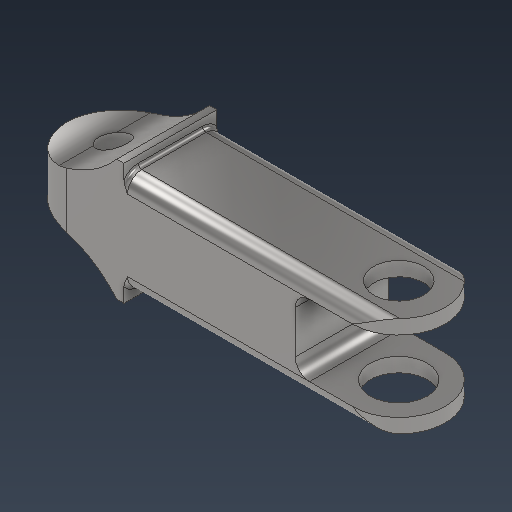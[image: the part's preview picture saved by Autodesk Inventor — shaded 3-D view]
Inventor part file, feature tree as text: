
AUTODESK INVENTOR PART (.ipt)
format: ipt  version: 2021 (Build 250183000, 183)  size: 280,576 bytes
history: native  units: mm
features: sketch x8, extrude x5, fillet x4, hole x3, other x2, mirror x1, projected_geometry x1
ambient origin geometry x8: Origin, YZ Plane, XZ Plane, XY Plane, X Axis, Y Axis, Z Axis, Center Point
bodies: Solid1 (feature_tree)
feature tree (24):
  extrude  "Extrusion1"  Depth=6.5mm
  sketch  "Sketch2"  dims[d4=40.0mm d5=20.0mm]
  other  "midPlane"
  extrude  "Extrusion4"  Depth=20.0mm
  hole  "Hole2"  [1 undecoded]
  sketch  "Sketch8"  dims[d12=0.0mm d35=14.0mm]
  hole  "Hole3"  [1 undecoded]
  hole  "Hole4"  [1 undecoded]
  fillet  "Fillet3"  Radius=8.0mm
  extrude  "Extrusion7"  TaperAngle=0.0deg  [1 undecoded]
  extrude  "Extrusion8"  Depth=0.5mm
  extrude  "Extrusion9"  Depth=0.5mm
  other  "lateralPlane"
  fillet  "Fillet6"  Radius=1.0mm
  mirror  "Mirror1"
  fillet  "Fillet8"  Radius=1.5mm
  fillet  "Fillet7"  Radius=1.5mm
  sketch  "Sketch1"  dims[d0=13.0mm d2=6.5mm]
  sketch  "Sketch5"  dims[d6=14.0mm d7=0.0mm d9=0.0mm]
  sketch  "Sketch9"  dims[d36=10.0mm d37=2.0mm d38=8.0mm]
  sketch  "Sketch10"  dims[d39=20.0mm d40=0.0mm d41=0.0mm]
  sketch  "Sketch11"  dims[d42=5.0mm d43=6.0mm d44=7.0mm d45=2.0mm d46=90.0deg d47=8.0mm d48=0.0mm]
  projected_geometry  "Projected Loop1"
  sketch  "Sketch12"  dims[d55=6.0mm d56=6.0mm d57=8.0mm d58=2.0mm d59=90.0deg d60=8.0mm d61=0.0mm d62=4.0mm d63=6.0mm d64=8.0mm d65=2.0mm d66=90.0deg d67=8.0mm d68=0.0mm d69=2.0mm d70=7.0mm d71=1.0mm d72=1.5mm d73=0.0mm d75=1.5mm d76=0.0mm d78=25.0mm d79=14.0mm d80=25.0mm d81=6.0mm d82=4.0mm d83=0.0mm d84=0.0mm d85=15.0mm d86=0.5mm d87=2.0mm]
note: 4 required parameter values undecoded (feature->parameter linkage not recoverable at this tier; creation-order binding heuristic only, values carry confidence <= 0.55)
